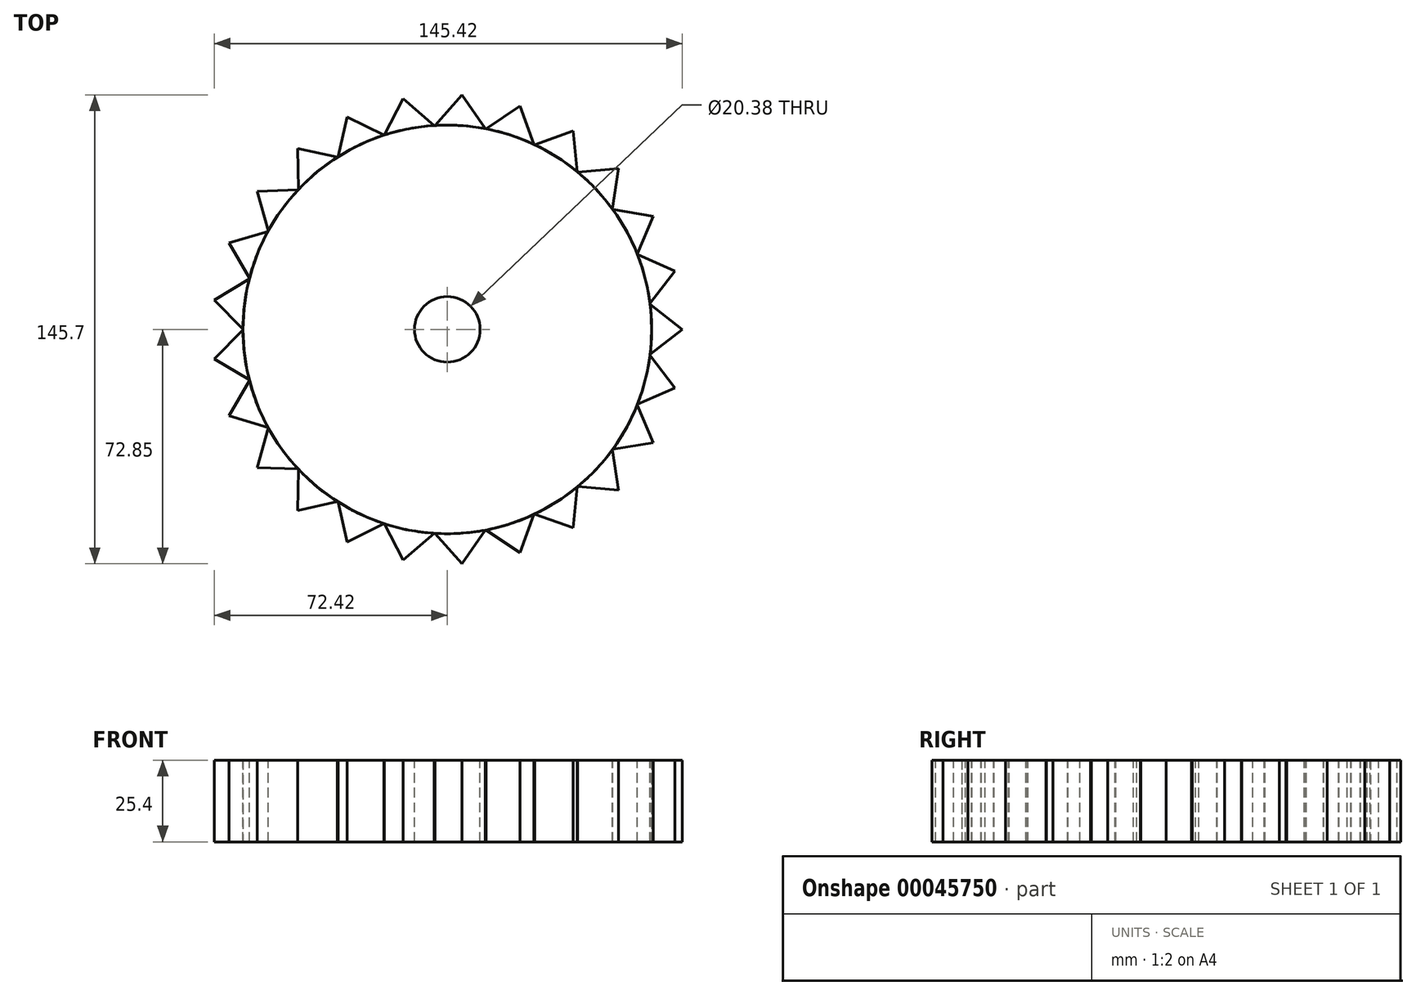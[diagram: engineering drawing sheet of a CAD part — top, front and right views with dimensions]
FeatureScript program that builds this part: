
annotation { "Feature Type Name" : "Feature", "Feature Type Description" : "" }
export const myFeature = defineFeature(function(context is Context, id is Id, definition is map)
    precondition{}
    {
        {
            var Q0;
            Q0=qCreatedBy(makeId("Top.planeOp"),FACE);
            var sketch = newSketch(context, id + "F0", { "sketchPlane" : qUnion([Q0])});
            skCircle(sketch, "E0", {"center": v(0, 0) * mm, "radius": 63.5 * mm});
            skSolve(sketch);
        }
        {
            var Q0;
            Q0=makeQuery(id+"F0.imprint","IMPRINT",FACE,{"disambiguationData":[TD([[makeQuery(id+"F0.imprint","IMPRINT",EDGE,{"derivedFrom":sQuery(id+"F0.wireOp",EDGE,"E0")}),1.0]])]});
            extrude(context, id + "F1", {"entities" : qUnion([Q0]), "endBound" : BoundingType.SYMMETRIC, "depth" : 25.4 * mm});
        }
        {
            var Q0;
            Q0=makeQuery(id+"F1.opExtrude","CAP_FACE",FACE,{"disambiguationData":[OSD([sQuery(id+"F0.wireOp",EDGE,"E0")])],"isStart":false});
            var sketch = newSketch(context, id + "F2", { "sketchPlane" : qUnion([Q0])});
            skCircle(sketch, "E1", {"center": v(0, 0) * mm, "radius": 10.2 * mm});
            skSolve(sketch);
        }
        {
            var Q0;
            Q0 = qSketchRegion(id + "F2", true);
            var Q1;
            Q1=makeQuery(id+"F1.opExtrude","CAP_FACE",FACE,{"disambiguationData":[OSD([sQuery(id+"F0.wireOp",EDGE,"E0")])],"isStart":true});
            extrude(context, id + "F3", {"entities" : qUnion([Q0]), "operationType" : NewBodyOperationType.REMOVE, "endBound" : BoundingType.UP_TO_SURFACE, "oppositeDirection" : true, "endBoundEntityFace" : qUnion([Q1]), "depth" : 34.2 * mm});
        }
        {
            var Q0;
            Q0=makeQuery(id+"F1.opExtrude","CAP_FACE",FACE,{"disambiguationData":[OSD([sQuery(id+"F0.wireOp",EDGE,"E0")])],"isStart":false});
            var sketch = newSketch(context, id + "F4", { "sketchPlane" : qUnion([Q0])});
            skArc(sketch, "E2.0", {"start": v(63.01, -7.85) * mm, "mid": v(63.5, 0) * mm, "end": v(63.01, 7.85) * mm});
            skLineSegment(sketch, "E3", {"start": v(63.01, 7.85) * mm, "end": v(73, 0) * mm});
            skLineSegment(sketch, "E4", {"start": v(73, 0) * mm, "end": v(63.01, -7.85) * mm});
            skSolve(sketch);
        }
        {
            var Q0;
            Q0=makeQuery(id+"F4.imprint","IMPRINT",FACE,{"disambiguationData":[TD([[makeQuery(id+"F4.imprint","IMPRINT",EDGE,{"derivedFrom":sQuery(id+"F4.wireOp",EDGE,"E2.0")}),-1.0]])]});
            var Q1;
            Q1=makeQuery(id+"F1.opExtrude","CAP_FACE",FACE,{"disambiguationData":[OSD([sQuery(id+"F0.wireOp",EDGE,"E0")])],"isStart":true});
            extrude(context, id + "F5", {"entities" : qUnion([Q0]), "endBound" : BoundingType.UP_TO_SURFACE, "oppositeDirection" : true, "endBoundEntityFace" : qUnion([Q1]), "depth" : 25.4 * mm});
        }
        {
            var Q0;
            Q0=makeQuery(id+"F5.opExtrude","SWEPT_BODY",BODY,{"disambiguationData":[OSD([sQuery(id+"F4.wireOp",EDGE,"E2.0"),sQuery(id+"F4.wireOp",EDGE,"E3"),sQuery(id+"F4.wireOp",EDGE,"E4")])]});
            var Q1;
            Q1=makeQuery(id+"F1.opExtrude","CAP_EDGE",EDGE,{"disambiguationData":[OSD([sQuery(id+"F0.wireOp",EDGE,"E0")])],"isStart":false});
            circularPattern(context, id + "F6", {"entities" : qUnion([Q0]), "axis" : qUnion([Q1]), "angle" : 360 * degree, "instanceCount" : 25, "equalSpace" : true});
        }
    });
